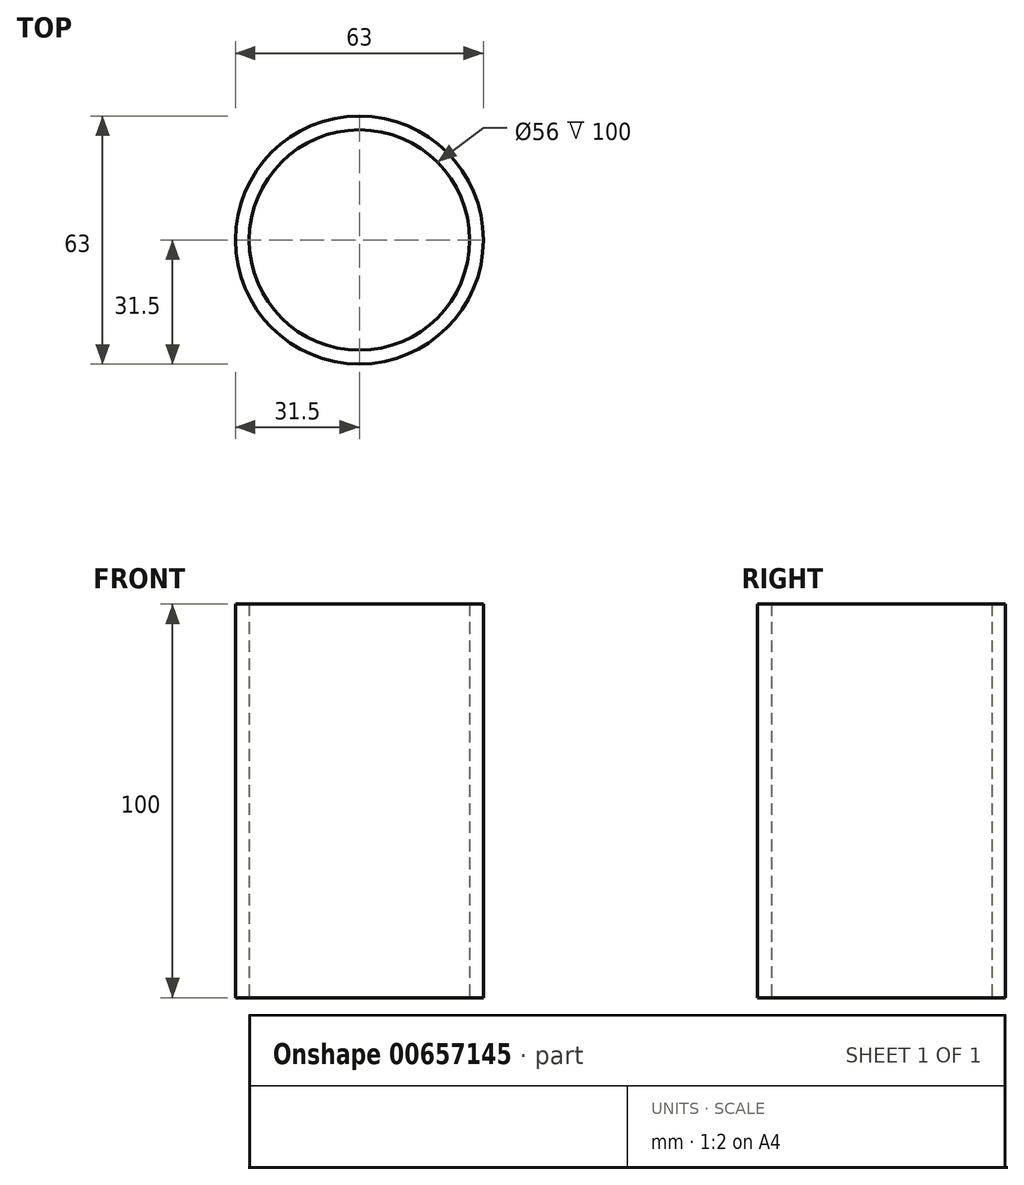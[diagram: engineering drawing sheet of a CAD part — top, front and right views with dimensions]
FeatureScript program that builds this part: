
annotation { "Feature Type Name" : "Feature", "Feature Type Description" : "" }
export const myFeature = defineFeature(function(context is Context, id is Id, definition is map)
    precondition{}
    {
        {
            var Q0;
            Q0=qCreatedBy(makeId("Top.planeOp"),FACE);
            var sketch = newSketch(context, id + "F0", { "sketchPlane" : qUnion([Q0])});
            skCircle(sketch, "E0", {"center": v(0, 0) * mm, "radius": 31.5 * mm});
            skCircle(sketch, "E1", {"center": v(0, 0) * mm, "radius": 28 * mm});
            skSolve(sketch);
        }
        {
            assignVariable(context, id + "F1", {"name" : "L", "anyValue" : 100});
        }
        {
            var Q0;
            Q0=makeQuery(id+"F0.imprint","IMPRINT",FACE,{"disambiguationData":[TD([[makeQuery(id+"F0.imprint","IMPRINT",EDGE,{"derivedFrom":sQuery(id+"F0.wireOp",EDGE,"E0")}),1.0]])]});
            extrude(context, id + "F2", {"entities" : qUnion([Q0]), "depth" : (getVariable(context, 'L')) * mm, "offsetDistance" : 25 * mm});
        }
    });
